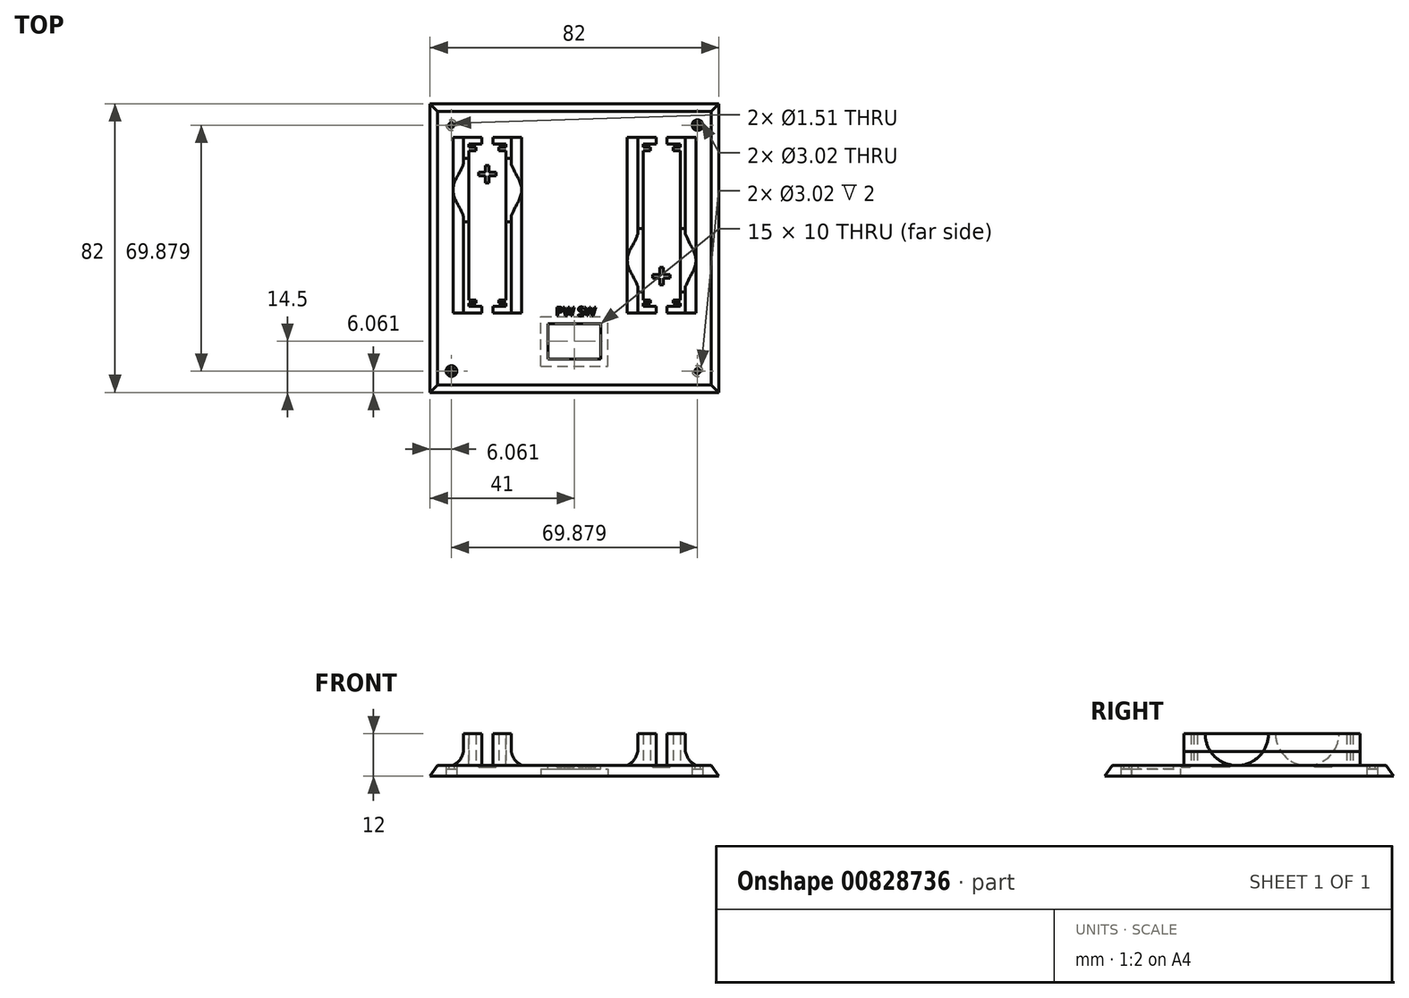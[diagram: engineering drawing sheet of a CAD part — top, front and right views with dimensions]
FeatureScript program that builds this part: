
annotation { "Feature Type Name" : "Feature", "Feature Type Description" : "" }
export const myFeature = defineFeature(function(context is Context, id is Id, definition is map)
    precondition{}
    {
        {
            assignVariable(context, id + "F0", {"name" : "Hollow", "anyValue" : 82});
        }
        {
            assignVariable(context, id + "F1", {"name" : "BaseThicknes", "anyValue" : 3});
        }
        {
            var Q0;
            Q0=qCreatedBy(makeId("Top.planeOp"),FACE);
            cPlane(context, id + "F2", {"entities" : qUnion([Q0]), "cplaneType" : CPlaneType.OFFSET, "offset" : (sqrt((sqrt((getVariable(context, 'Hollow') * getVariable(context, 'Hollow')) - ((getVariable(context, 'Hollow') / 2) * (getVariable(context, 'Hollow') / 2)))) * (sqrt((getVariable(context, 'Hollow') * getVariable(context, 'Hollow')) - ((getVariable(context, 'Hollow') / 2) * (getVariable(context, 'Hollow') / 2)))) - ((getVariable(context, 'Hollow') / 2) * (getVariable(context, 'Hollow') / 2)))) * mm, "width" : 150 * mm, "height" : 150 * mm});
        }
        {
            var Q0;
            Q0=qCreatedBy(id+"F2.planeOp",FACE);
            var sketch = newSketch(context, id + "F3", { "sketchPlane" : qUnion([Q0])});
            skPoint(sketch, "E0", {"position": v(0, 0) * mm});
            skSolve(sketch);
        }
        {
            var Q0;
            Q0=qCreatedBy(makeId("Top.planeOp"),FACE);
            var sketch = newSketch(context, id + "F4", { "sketchPlane" : qUnion([Q0])});
            skLineSegment(sketch, "E1.bottom", {"start": v(-41, 41) * mm, "end": v(41, 41) * mm});
            skLineSegment(sketch, "E1.top", {"start": v(-41, -41) * mm, "end": v(41, -41) * mm});
            skLineSegment(sketch, "E1.left", {"start": v(-41, 41) * mm, "end": v(-41, -41) * mm});
            skLineSegment(sketch, "E1.right", {"start": v(41, 41) * mm, "end": v(41, -41) * mm});
            skSolve(sketch);
        }
        {
            var Q0;
            Q0 = qSketchRegion(id + "F4", true);
            extrude(context, id + "F5", {"entities" : qUnion([Q0]), "depth" : (getVariable(context, 'BaseThicknes')) * mm, "offsetDistance" : 25 * mm});
        }
        {
            var Q1;
            Q1=makeQuery(id+"F5.opExtrude","CAP_FACE",FACE,{"disambiguationData":[OSD([sQuery(id+"F4.wireOp",EDGE,"E1.bottom"),sQuery(id+"F4.wireOp",EDGE,"E1.top"),sQuery(id+"F4.wireOp",EDGE,"E1.left"),sQuery(id+"F4.wireOp",EDGE,"E1.right")])],"isStart":true});
            var Q2;
            Q2=sQuery(id+"F3.wireOp",VERTEX,"E0");
            loft(context, id + "F6", {"operationType" : NewBodyOperationType.INTERSECT, "sheetProfilesArray" : [{ "sheetProfileEntities" : qUnion([Q1]) }, { "sheetProfileEntities" : qUnion([Q2]) }]});
        }
        {
            var Q0;
            Q0=makeQuery(id+"F5.opExtrude","CAP_FACE",FACE,{"disambiguationData":[OSD([sQuery(id+"F4.wireOp",EDGE,"E1.bottom"),sQuery(id+"F4.wireOp",EDGE,"E1.top"),sQuery(id+"F4.wireOp",EDGE,"E1.left"),sQuery(id+"F4.wireOp",EDGE,"E1.right")])],"isStart":true});
            var sketch = newSketch(context, id + "F7", { "sketchPlane" : qUnion([Q0])});
            skCircle(sketch, "E2", {"center": v(-34.94, -34.94) * mm, "radius": 0.76 * mm});
            skCircle(sketch, "E3.MirrorC", {"center": v(34.94, -34.94) * mm, "radius": 0.76 * mm});
            skCircle(sketch, "E4.MirrorC", {"center": v(34.94, 34.94) * mm, "radius": 0.76 * mm});
            skCircle(sketch, "E5.MirrorC", {"center": v(-34.94, 34.94) * mm, "radius": 0.76 * mm});
            skCircle(sketch, "E6", {"center": v(-34.94, -34.94) * mm, "radius": 1.51 * mm});
            skCircle(sketch, "E7.MirrorC", {"center": v(-34.94, 34.94) * mm, "radius": 1.51 * mm});
            skCircle(sketch, "E8.MirrorC", {"center": v(34.94, -34.94) * mm, "radius": 1.51 * mm});
            skCircle(sketch, "E9.MirrorC", {"center": v(34.94, 34.94) * mm, "radius": 1.51 * mm});
            skSolve(sketch);
        }
        {
            var Q0;
            Q0=makeQuery(id+"F7.imprint","IMPRINT",FACE,{"disambiguationData":[TD([[makeQuery(id+"F7.imprint","IMPRINT",EDGE,{"derivedFrom":sQuery(id+"F7.wireOp",EDGE,"E2")}),1.0]])]});
            var Q1;
            Q1=makeQuery(id+"F7.imprint","IMPRINT",FACE,{"disambiguationData":[TD([[makeQuery(id+"F7.imprint","IMPRINT",EDGE,{"derivedFrom":sQuery(id+"F7.wireOp",EDGE,"E5.MirrorC")}),-1.0]])]});
            var Q2;
            Q2=makeQuery(id+"F7.imprint","IMPRINT",FACE,{"disambiguationData":[TD([[makeQuery(id+"F7.imprint","IMPRINT",EDGE,{"derivedFrom":sQuery(id+"F7.wireOp",EDGE,"E4.MirrorC")}),1.0]])]});
            var Q3;
            Q3=makeQuery(id+"F7.imprint","IMPRINT",FACE,{"disambiguationData":[TD([[makeQuery(id+"F7.imprint","IMPRINT",EDGE,{"derivedFrom":sQuery(id+"F7.wireOp",EDGE,"E3.MirrorC")}),-1.0]])]});
            extrude(context, id + "F8", {"entities" : qUnion([Q0, Q1, Q2, Q3]), "operationType" : NewBodyOperationType.REMOVE, "oppositeDirection" : true, "depth" : 25 * mm, "offsetDistance" : 25 * mm});
        }
        {
            var Q0;
            Q0=makeQuery(id+"F7.imprint","IMPRINT",FACE,{"disambiguationData":[TD([[makeQuery(id+"F7.imprint","IMPRINT",EDGE,{"derivedFrom":sQuery(id+"F7.wireOp",EDGE,"E5.MirrorC")}),1.0]])]});
            var Q1;
            Q1=makeQuery(id+"F7.imprint","IMPRINT",FACE,{"disambiguationData":[TD([[makeQuery(id+"F7.imprint","IMPRINT",EDGE,{"derivedFrom":sQuery(id+"F7.wireOp",EDGE,"E4.MirrorC")}),-1.0]])]});
            var Q2;
            Q2=makeQuery(id+"F7.imprint","IMPRINT",FACE,{"disambiguationData":[TD([[makeQuery(id+"F7.imprint","IMPRINT",EDGE,{"derivedFrom":sQuery(id+"F7.wireOp",EDGE,"E2")}),-1.0]])]});
            var Q3;
            Q3=makeQuery(id+"F7.imprint","IMPRINT",FACE,{"disambiguationData":[TD([[makeQuery(id+"F7.imprint","IMPRINT",EDGE,{"derivedFrom":sQuery(id+"F7.wireOp",EDGE,"E3.MirrorC")}),1.0]])]});
            extrude(context, id + "F9", {"entities" : qUnion([Q0, Q1, Q2, Q3]), "operationType" : NewBodyOperationType.REMOVE, "oppositeDirection" : true, "depth" : 2 * mm, "offsetDistance" : 25 * mm});
        }
        {
            var Q0;
            Q0=makeQuery(id+"F5.opExtrude","CAP_FACE",FACE,{"disambiguationData":[OSD([sQuery(id+"F4.wireOp",EDGE,"E1.bottom"),sQuery(id+"F4.wireOp",EDGE,"E1.top"),sQuery(id+"F4.wireOp",EDGE,"E1.left"),sQuery(id+"F4.wireOp",EDGE,"E1.right")])],"isStart":false});
            var sketch = newSketch(context, id + "F10", { "sketchPlane" : qUnion([Q0])});
            skLineSegment(sketch, "E10.bottom", {"start": v(-30, 29.5) * mm, "end": v(-26.3, 29.5) * mm});
            skLineSegment(sketch, "E10.top", {"start": v(-30, -16.5) * mm, "end": v(-26.3, -16.5) * mm});
            skLineSegment(sketch, "E10.left", {"start": v(-30, 29.5) * mm, "end": v(-30, -16.5) * mm});
            skLineSegment(sketch, "E10.right", {"start": v(-19.5, 29.5) * mm, "end": v(-19.5, -16.5) * mm});
            skLineSegment(sketch, "E11.bottom", {"start": v(-31.5, 31.5) * mm, "end": v(-26.3, 31.5) * mm});
            skLineSegment(sketch, "E11.top", {"start": v(-31.5, -18.5) * mm, "end": v(-18, -18.5) * mm});
            skLineSegment(sketch, "E11.left", {"start": v(-31.5, 31.5) * mm, "end": v(-31.5, -18.5) * mm});
            skLineSegment(sketch, "E11.right", {"start": v(-18, 31.5) * mm, "end": v(-18, -18.5) * mm});
            skLineSegment(sketch, "E12", {"start": v(-30, 27.7) * mm, "end": v(-28, 27.7) * mm});
            skLineSegment(sketch, "E13", {"start": v(-30, 28.7) * mm, "end": v(-28, 28.7) * mm});
            skLineSegment(sketch, "E14.left", {"start": v(-21.5, 28.7) * mm, "end": v(-21.5, 27.7) * mm});
            skLineSegment(sketch, "E14.right", {"start": v(-28, 28.7) * mm, "end": v(-28, 27.7) * mm});
            skLineSegment(sketch, "E15", {"start": v(-18, 6.5) * mm, "end": v(-31.5, 6.5) * mm, "construction": true});
            skLineSegment(sketch, "E16.trimOffspring", {"start": v(-21.5, 27.7) * mm, "end": v(-19.5, 27.7) * mm});
            skLineSegment(sketch, "E17.trimOffspring", {"start": v(-21.5, 28.7) * mm, "end": v(-19.5, 28.7) * mm});
            skLineSegment(sketch, "E18.MirrorCS", {"start": v(-30, -15.7) * mm, "end": v(-28, -15.7) * mm});
            skLineSegment(sketch, "E19.MirrorCS", {"start": v(-30, -14.7) * mm, "end": v(-28, -14.7) * mm});
            skLineSegment(sketch, "E20.MirrorCS", {"start": v(-21.5, -15.7) * mm, "end": v(-21.5, -14.7) * mm});
            skLineSegment(sketch, "E21.MirrorCS", {"start": v(-21.5, -15.7) * mm, "end": v(-19.5, -15.7) * mm});
            skLineSegment(sketch, "E22.MirrorCS", {"start": v(-21.5, -14.7) * mm, "end": v(-19.5, -14.7) * mm});
            skLineSegment(sketch, "E23.MirrorCS", {"start": v(-28, -15.7) * mm, "end": v(-28, -14.7) * mm});
            skLineSegment(sketch, "E24", {"start": v(-26.3, 31.5) * mm, "end": v(-26.3, 29.5) * mm});
            skLineSegment(sketch, "E25", {"start": v(-23.2, 31.5) * mm, "end": v(-23.2, 29.5) * mm});
            skLineSegment(sketch, "E26.trimOffspring", {"start": v(-23.2, 31.5) * mm, "end": v(-18, 31.5) * mm});
            skLineSegment(sketch, "E27.trimOffspring", {"start": v(-23.2, 29.5) * mm, "end": v(-19.5, 29.5) * mm});
            skLineSegment(sketch, "E28.MirrorCS", {"start": v(-26.3, -18.5) * mm, "end": v(-26.3, -16.5) * mm});
            skLineSegment(sketch, "E29.MirrorCS", {"start": v(-23.2, -18.5) * mm, "end": v(-23.2, -16.5) * mm});
            skLineSegment(sketch, "E30.trimOffspring", {"start": v(-23.2, -16.5) * mm, "end": v(-19.5, -16.5) * mm});
            skLineSegment(sketch, "E31.MirrorCS", {"start": v(21.5, 28.7) * mm, "end": v(21.5, 27.7) * mm});
            skLineSegment(sketch, "E32.MirrorCS", {"start": v(21.5, 28.7) * mm, "end": v(19.5, 28.7) * mm});
            skLineSegment(sketch, "E33.MirrorCS", {"start": v(23.2, 29.5) * mm, "end": v(19.5, 29.5) * mm});
            skLineSegment(sketch, "E34.MirrorCS", {"start": v(23.2, 31.5) * mm, "end": v(23.2, 29.5) * mm});
            skLineSegment(sketch, "E35.MirrorCS", {"start": v(28, -15.7) * mm, "end": v(28, -14.7) * mm});
            skLineSegment(sketch, "E36.MirrorCS", {"start": v(21.5, -15.7) * mm, "end": v(19.5, -15.7) * mm});
            skLineSegment(sketch, "E37.MirrorCS", {"start": v(23.2, -16.5) * mm, "end": v(19.5, -16.5) * mm});
            skLineSegment(sketch, "E38.MirrorCS", {"start": v(30, -15.7) * mm, "end": v(28, -15.7) * mm});
            skLineSegment(sketch, "E39.MirrorCS", {"start": v(21.5, -14.7) * mm, "end": v(19.5, -14.7) * mm});
            skLineSegment(sketch, "E40.MirrorCS", {"start": v(30, 29.5) * mm, "end": v(26.3, 29.5) * mm});
            skLineSegment(sketch, "E41.MirrorCS", {"start": v(30, 28.7) * mm, "end": v(28, 28.7) * mm});
            skLineSegment(sketch, "E42.MirrorCS", {"start": v(30, -16.5) * mm, "end": v(26.3, -16.5) * mm});
            skLineSegment(sketch, "E43.MirrorCS", {"start": v(26.3, 31.5) * mm, "end": v(26.3, 29.5) * mm});
            skLineSegment(sketch, "E44.MirrorCS", {"start": v(21.5, -15.7) * mm, "end": v(21.5, -14.7) * mm});
            skLineSegment(sketch, "E45.MirrorCS", {"start": v(28, 28.7) * mm, "end": v(28, 27.7) * mm});
            skLineSegment(sketch, "E46.MirrorCS", {"start": v(30, -14.7) * mm, "end": v(28, -14.7) * mm});
            skLineSegment(sketch, "E47.MirrorCS", {"start": v(31.5, 31.5) * mm, "end": v(26.3, 31.5) * mm});
            skLineSegment(sketch, "E48.MirrorCS", {"start": v(21.5, 27.7) * mm, "end": v(19.5, 27.7) * mm});
            skLineSegment(sketch, "E49.MirrorCS", {"start": v(23.2, -18.5) * mm, "end": v(23.2, -16.5) * mm});
            skLineSegment(sketch, "E50.MirrorCS", {"start": v(30, 27.7) * mm, "end": v(28, 27.7) * mm});
            skLineSegment(sketch, "E51.MirrorCS", {"start": v(26.3, -18.5) * mm, "end": v(26.3, -16.5) * mm});
            skLineSegment(sketch, "E52.MirrorCS", {"start": v(23.2, 31.5) * mm, "end": v(18, 31.5) * mm});
            skLineSegment(sketch, "E53.MirrorCS", {"start": v(31.5, 31.5) * mm, "end": v(31.5, -18.5) * mm});
            skLineSegment(sketch, "E54.MirrorCS", {"start": v(30, 29.5) * mm, "end": v(30, -16.5) * mm});
            skLineSegment(sketch, "E55.MirrorCS", {"start": v(31.5, -18.5) * mm, "end": v(18, -18.5) * mm});
            skLineSegment(sketch, "E56.MirrorCS", {"start": v(19.5, 29.5) * mm, "end": v(19.5, -16.5) * mm});
            skLineSegment(sketch, "E57.MirrorCS", {"start": v(18, 31.5) * mm, "end": v(18, -18.5) * mm});
            skLineSegment(sketch, "E58.MirrorCS", {"start": v(18, 6.5) * mm, "end": v(31.5, 6.5) * mm, "construction": true});
            skSolve(sketch);
        }
        {
            var Q0;
            {var subQ5=sQuery(id+"F10.wireOp",EDGE,"E33.MirrorCS");Q0=makeQuery(id+"F10.imprint","IMPRINT",FACE,{"disambiguationData":[TD([[makeQuery(id+"F10.imprint","IMPRINT",EDGE,{"derivedFrom":subQ5}),-1.0]])]});}
            var Q1;
            {var subQ6=sQuery(id+"F10.wireOp",EDGE,"E40.MirrorCS");Q1=makeQuery(id+"F10.imprint","IMPRINT",FACE,{"disambiguationData":[TD([[makeQuery(id+"F10.imprint","IMPRINT",EDGE,{"derivedFrom":subQ6}),-1.0]])]});}
            var Q2;
            Q2=makeQuery(id+"F10.imprint","IMPRINT",FACE,{"disambiguationData":[TD([[makeQuery(id+"F10.imprint","IMPRINT",EDGE,{"derivedFrom":sQuery(id+"F10.wireOp",EDGE,"E31.MirrorCS")}),-1.0]])]});
            var Q3;
            {var subQ0=sQuery(id+"F10.wireOp",EDGE,"E41.MirrorCS");Q3=makeQuery(id+"F10.imprint","IMPRINT",FACE,{"disambiguationData":[TD([[makeQuery(id+"F10.imprint","IMPRINT",EDGE,{"derivedFrom":subQ0}),1.0]])]});}
            var Q4;
            {var subQ0=sQuery(id+"F10.wireOp",EDGE,"E36.MirrorCS");Q4=makeQuery(id+"F10.imprint","IMPRINT",FACE,{"disambiguationData":[TD([[makeQuery(id+"F10.imprint","IMPRINT",EDGE,{"derivedFrom":subQ0}),-1.0]])]});}
            var Q5;
            Q5=makeQuery(id+"F10.imprint","IMPRINT",FACE,{"disambiguationData":[TD([[makeQuery(id+"F10.imprint","IMPRINT",EDGE,{"derivedFrom":sQuery(id+"F10.wireOp",EDGE,"E35.MirrorCS")}),-1.0]])]});
            var Q6;
            Q6=makeQuery(id+"F10.imprint","IMPRINT",FACE,{"disambiguationData":[TD([[makeQuery(id+"F10.imprint","IMPRINT",EDGE,{"derivedFrom":sQuery(id+"F10.wireOp",EDGE,"E20.MirrorCS")}),-1.0]])]});
            var Q7;
            {var subQ0=sQuery(id+"F10.wireOp",EDGE,"E18.MirrorCS");Q7=makeQuery(id+"F10.imprint","IMPRINT",FACE,{"disambiguationData":[TD([[makeQuery(id+"F10.imprint","IMPRINT",EDGE,{"derivedFrom":subQ0}),1.0]])]});}
            var Q8;
            {var subQ6=sQuery(id+"F10.wireOp",EDGE,"E10.bottom");Q8=makeQuery(id+"F10.imprint","IMPRINT",FACE,{"disambiguationData":[TD([[makeQuery(id+"F10.imprint","IMPRINT",EDGE,{"derivedFrom":subQ6}),1.0]])]});}
            var Q9;
            {var subQ0=sQuery(id+"F10.wireOp",EDGE,"E11.right");Q9=makeQuery(id+"F10.imprint","IMPRINT",FACE,{"disambiguationData":[TD([[makeQuery(id+"F10.imprint","IMPRINT",EDGE,{"derivedFrom":subQ0}),-1.0]])]});}
            var Q10;
            {var subQ0=sQuery(id+"F10.wireOp",EDGE,"E12");Q10=makeQuery(id+"F10.imprint","IMPRINT",FACE,{"disambiguationData":[TD([[makeQuery(id+"F10.imprint","IMPRINT",EDGE,{"derivedFrom":subQ0}),1.0]])]});}
            var Q11;
            Q11=makeQuery(id+"F10.imprint","IMPRINT",FACE,{"disambiguationData":[TD([[makeQuery(id+"F10.imprint","IMPRINT",EDGE,{"derivedFrom":sQuery(id+"F10.wireOp",EDGE,"E14.left")}),1.0]])]});
            extrude(context, id + "F11", {"entities" : qUnion([Q0, Q1, Q2, Q3, Q4, Q5, Q6, Q7, Q8, Q9, Q10, Q11]), "operationType" : NewBodyOperationType.ADD, "depth" : 9 * mm, "offsetDistance" : 25 * mm});
        }
        {
            var Q0;
            Q0=qCreatedBy(makeId("Front.planeOp"),FACE);
            var sketch = newSketch(context, id + "F12", { "sketchPlane" : qUnion([Q0])});
            skLineSegment(sketch, "E59", {"start": v(-31.5, 3) * mm, "end": v(-34.5, 3) * mm});
            skLineSegment(sketch, "E60", {"start": v(-31.5, 3) * mm, "end": v(-31.5, 7) * mm});
            skPoint(sketch, "E61", {"position": v(-34.5, 3) * mm});
            skFitSpline(sketch, "E62", {"points": [v(-31.5, 7) * mm, v(-32.53, 4.65) * mm, v(-34.5, 3) * mm], "startDerivative": vector(-1.67, -5.36) * mm, "endDerivative": vector(-4.69, -2.88) * mm});
            skLineSegment(sketch, "E63", {"start": v(-24.75, 13.95) * mm, "end": v(-24.75, 2.35) * mm, "construction": true});
            skFitSpline(sketch, "E64.MirrorCS", {"points": [v(-18, 7) * mm, v(-16.97, 4.65) * mm, v(-15, 3) * mm], "startDerivative": vector(1.67, -5.36) * mm, "endDerivative": vector(4.69, -2.88) * mm});
            skFitSpline(sketch, "E65.MirrorCS", {"points": [v(18, 7) * mm, v(16.97, 4.65) * mm, v(15, 3) * mm], "startDerivative": vector(-1.67, -5.36) * mm, "endDerivative": vector(-4.69, -2.88) * mm});
            skFitSpline(sketch, "E66.MirrorCS", {"points": [v(31.5, 7) * mm, v(32.53, 4.65) * mm, v(34.5, 3) * mm], "startDerivative": vector(1.67, -5.36) * mm, "endDerivative": vector(4.69, -2.88) * mm});
            skLineSegment(sketch, "E67.MirrorCS", {"start": v(-18, 3) * mm, "end": v(-15, 3) * mm});
            skLineSegment(sketch, "E68.MirrorCS", {"start": v(18, 3) * mm, "end": v(15, 3) * mm});
            skLineSegment(sketch, "E69.MirrorCS", {"start": v(31.5, 3) * mm, "end": v(34.5, 3) * mm});
            skLineSegment(sketch, "E70.MirrorCS", {"start": v(-18, 3) * mm, "end": v(-18, 7) * mm});
            skLineSegment(sketch, "E71.MirrorCS", {"start": v(18, 3) * mm, "end": v(18, 7) * mm});
            skLineSegment(sketch, "E72.MirrorCS", {"start": v(31.5, 3) * mm, "end": v(31.5, 7) * mm});
            skSolve(sketch);
        }
        {
            var Q0;
            Q0 = qSketchRegion(id + "F12", true);
            extrude(context, id + "F13", {"entities" : qUnion([Q0]), "operationType" : NewBodyOperationType.ADD, "depth" : 18.5 * mm, "offsetDistance" : 25 * mm, "hasSecondDirection" : true, "secondDirectionOppositeDirection" : true, "secondDirectionDepth" : 31.5 * mm});
        }
        {
            var Q0;
            Q0=qCreatedBy(makeId("Right.planeOp"),FACE);
            var sketch = newSketch(context, id + "F14", { "sketchPlane" : qUnion([Q0])});
            skCircle(sketch, "E73", {"center": v(16.5, 12) * mm, "radius": 9 * mm});
            skCircle(sketch, "E74", {"center": v(-3.5, 12) * mm, "radius": 9 * mm});
            skSolve(sketch);
        }
        {
            var Q0;
            Q0=makeQuery(id+"F14.imprint","IMPRINT",FACE,{"disambiguationData":[TD([[makeQuery(id+"F14.imprint","IMPRINT",EDGE,{"derivedFrom":sQuery(id+"F14.wireOp",EDGE,"E73")}),1.0]])]});
            extrude(context, id + "F15", {"entities" : qUnion([Q0]), "operationType" : NewBodyOperationType.REMOVE, "oppositeDirection" : true, "depth" : 50 * mm, "offsetDistance" : 25 * mm});
        }
        {
            var Q0;
            Q0=makeQuery(id+"F14.imprint","IMPRINT",FACE,{"disambiguationData":[TD([[makeQuery(id+"F14.imprint","IMPRINT",EDGE,{"derivedFrom":sQuery(id+"F14.wireOp",EDGE,"E74")}),1.0]])]});
            extrude(context, id + "F16", {"entities" : qUnion([Q0]), "operationType" : NewBodyOperationType.REMOVE, "oppositeDirection" : true, "depth" : -50 * mm, "offsetDistance" : 25 * mm});
        }
        {
            var Q0;
            Q0=makeQuery(id+"F5.opExtrude","CAP_FACE",FACE,{"disambiguationData":[OSD([sQuery(id+"F4.wireOp",EDGE,"E1.bottom"),sQuery(id+"F4.wireOp",EDGE,"E1.top"),sQuery(id+"F4.wireOp",EDGE,"E1.left"),sQuery(id+"F4.wireOp",EDGE,"E1.right")])],"isStart":false});
            var sketch = newSketch(context, id + "F17", { "sketchPlane" : qUnion([Q0])});
            skLineSegment(sketch, "E75.bottom", {"start": v(-7.5, -21.5) * mm, "end": v(7.5, -21.5) * mm});
            skLineSegment(sketch, "E75.top", {"start": v(-7.5, -31.5) * mm, "end": v(7.5, -31.5) * mm});
            skLineSegment(sketch, "E75.left", {"start": v(-7.5, -21.5) * mm, "end": v(-7.5, -31.5) * mm});
            skLineSegment(sketch, "E75.right", {"start": v(7.5, -21.5) * mm, "end": v(7.5, -31.5) * mm});
            skSolve(sketch);
        }
        {
            var Q0;
            Q0 = qSketchRegion(id + "F17", true);
            extrude(context, id + "F18", {"entities" : qUnion([Q0]), "operationType" : NewBodyOperationType.REMOVE, "oppositeDirection" : true, "depth" : 25 * mm, "offsetDistance" : 25 * mm});
        }
        {
            var Q0;
            Q0=makeQuery(id+"F5.opExtrude","CAP_FACE",FACE,{"disambiguationData":[OSD([sQuery(id+"F4.wireOp",EDGE,"E1.bottom"),sQuery(id+"F4.wireOp",EDGE,"E1.top"),sQuery(id+"F4.wireOp",EDGE,"E1.left"),sQuery(id+"F4.wireOp",EDGE,"E1.right")])],"isStart":true});
            var sketch = newSketch(context, id + "F19", { "sketchPlane" : qUnion([Q0])});
            skLineSegment(sketch, "E76.bottom", {"start": v(-9.5, 33.5) * mm, "end": v(9.5, 33.5) * mm});
            skLineSegment(sketch, "E76.top", {"start": v(-9.5, 19.5) * mm, "end": v(9.5, 19.5) * mm});
            skLineSegment(sketch, "E76.left", {"start": v(-9.5, 33.5) * mm, "end": v(-9.5, 19.5) * mm});
            skLineSegment(sketch, "E76.right", {"start": v(9.5, 33.5) * mm, "end": v(9.5, 19.5) * mm});
            skSolve(sketch);
        }
        {
            var Q0;
            Q0 = qSketchRegion(id + "F19", true);
            extrude(context, id + "F20", {"entities" : qUnion([Q0]), "operationType" : NewBodyOperationType.REMOVE, "oppositeDirection" : true, "depth" : 2 * mm, "offsetDistance" : 25 * mm});
        }
        {
            var Q0;
            Q0=makeQuery(id+"F5.opExtrude","CAP_FACE",FACE,{"disambiguationData":[OSD([sQuery(id+"F4.wireOp",EDGE,"E1.bottom"),sQuery(id+"F4.wireOp",EDGE,"E1.top"),sQuery(id+"F4.wireOp",EDGE,"E1.left"),sQuery(id+"F4.wireOp",EDGE,"E1.right")])],"isStart":false});
            var sketch = newSketch(context, id + "F21", { "sketchPlane" : qUnion([Q0])});
            skLineSegment(sketch, "E77.bottom", {"start": v(-25.25, 23.5) * mm, "end": v(-24.25, 23.5) * mm});
            skLineSegment(sketch, "E77.top", {"start": v(-25.25, 18.5) * mm, "end": v(-24.25, 18.5) * mm});
            skLineSegment(sketch, "E77.left", {"start": v(-25.25, 23.5) * mm, "end": v(-25.25, 18.5) * mm});
            skLineSegment(sketch, "E77.right", {"start": v(-24.25, 23.5) * mm, "end": v(-24.25, 18.5) * mm});
            skLineSegment(sketch, "E78.bottom", {"start": v(-27.25, 21.5) * mm, "end": v(-22.25, 21.5) * mm});
            skLineSegment(sketch, "E78.top", {"start": v(-27.25, 20.5) * mm, "end": v(-22.25, 20.5) * mm});
            skLineSegment(sketch, "E78.left", {"start": v(-27.25, 21.5) * mm, "end": v(-27.25, 20.5) * mm});
            skLineSegment(sketch, "E78.right", {"start": v(-22.25, 21.5) * mm, "end": v(-22.25, 20.5) * mm});
            skLineSegment(sketch, "E79", {"start": v(-24.75, 32.18) * mm, "end": v(-24.75, -20.77) * mm, "construction": true});
            skLineSegment(sketch, "E80.bottom", {"start": v(24.2, -5.5) * mm, "end": v(25.2, -5.5) * mm});
            skLineSegment(sketch, "E80.top", {"start": v(24.2, -10.5) * mm, "end": v(25.2, -10.5) * mm});
            skLineSegment(sketch, "E80.left", {"start": v(24.2, -5.5) * mm, "end": v(24.2, -10.5) * mm});
            skLineSegment(sketch, "E80.right", {"start": v(25.2, -5.5) * mm, "end": v(25.2, -10.5) * mm});
            skLineSegment(sketch, "E81.bottom", {"start": v(22.2, -7.5) * mm, "end": v(27.2, -7.5) * mm});
            skLineSegment(sketch, "E81.top", {"start": v(22.2, -8.5) * mm, "end": v(27.2, -8.5) * mm});
            skLineSegment(sketch, "E81.left", {"start": v(22.2, -7.5) * mm, "end": v(22.2, -8.5) * mm});
            skLineSegment(sketch, "E81.right", {"start": v(27.2, -7.5) * mm, "end": v(27.2, -8.5) * mm});
            skLineSegment(sketch, "E82", {"start": v(24.7, 5.1) * mm, "end": v(24.7, -19.14) * mm, "construction": true});
            skText(sketch, "E83", { "text": "PW SW", "fontName": "OpenSans-Regular.ttf"});
            const initialGuessF21  = {"E83": [-0.00532, -0.01924, 1, 0, 0.00251]};
            skSetInitialGuess(sketch, initialGuessF21);
            skSolve(sketch);
        }
        {
            var Q0;
            Q0 = qSketchRegion(id + "F21", true);
            extrude(context, id + "F22", {"entities" : qUnion([Q0]), "operationType" : NewBodyOperationType.REMOVE, "oppositeDirection" : true, "depth" : .5 * mm, "offsetDistance" : 25 * mm});
        }
        {
            var Q0;
            Q0=makeQuery(id+"F21.imprint","IMPRINT",FACE,{"disambiguationData":[TD([[makeQuery(id+"F21.imprint","IMPRINT",EDGE,{"derivedFrom":sQuery(id+"F21.wireOp",EDGE,"E83.sketch_text.stroke-35")}),-1.0]])]});
            var Q1;
            Q1=makeQuery(id+"F21.imprint","IMPRINT",FACE,{"disambiguationData":[TD([[makeQuery(id+"F21.imprint","IMPRINT",EDGE,{"derivedFrom":sQuery(id+"F21.wireOp",EDGE,"E83.sketch_text.stroke-60")}),-1.0]])]});
            var Q2;
            Q2=makeQuery(id+"F21.imprint","IMPRINT",FACE,{"disambiguationData":[TD([[makeQuery(id+"F21.imprint","IMPRINT",EDGE,{"derivedFrom":sQuery(id+"F21.wireOp",EDGE,"E83.sketch_text.stroke-15")}),-1.0]])]});
            var Q3;
            Q3=makeQuery(id+"F21.imprint","IMPRINT",FACE,{"disambiguationData":[TD([[makeQuery(id+"F21.imprint","IMPRINT",EDGE,{"derivedFrom":sQuery(id+"F21.wireOp",EDGE,"E83.sketch_text.stroke-0")}),-1.0]])]});
            extrude(context, id + "F23", {"entities" : qUnion([Q0, Q1, Q2, Q3]), "operationType" : NewBodyOperationType.REMOVE, "oppositeDirection" : true, "depth" : .5 * mm, "offsetDistance" : 25 * mm});
        }
    });
